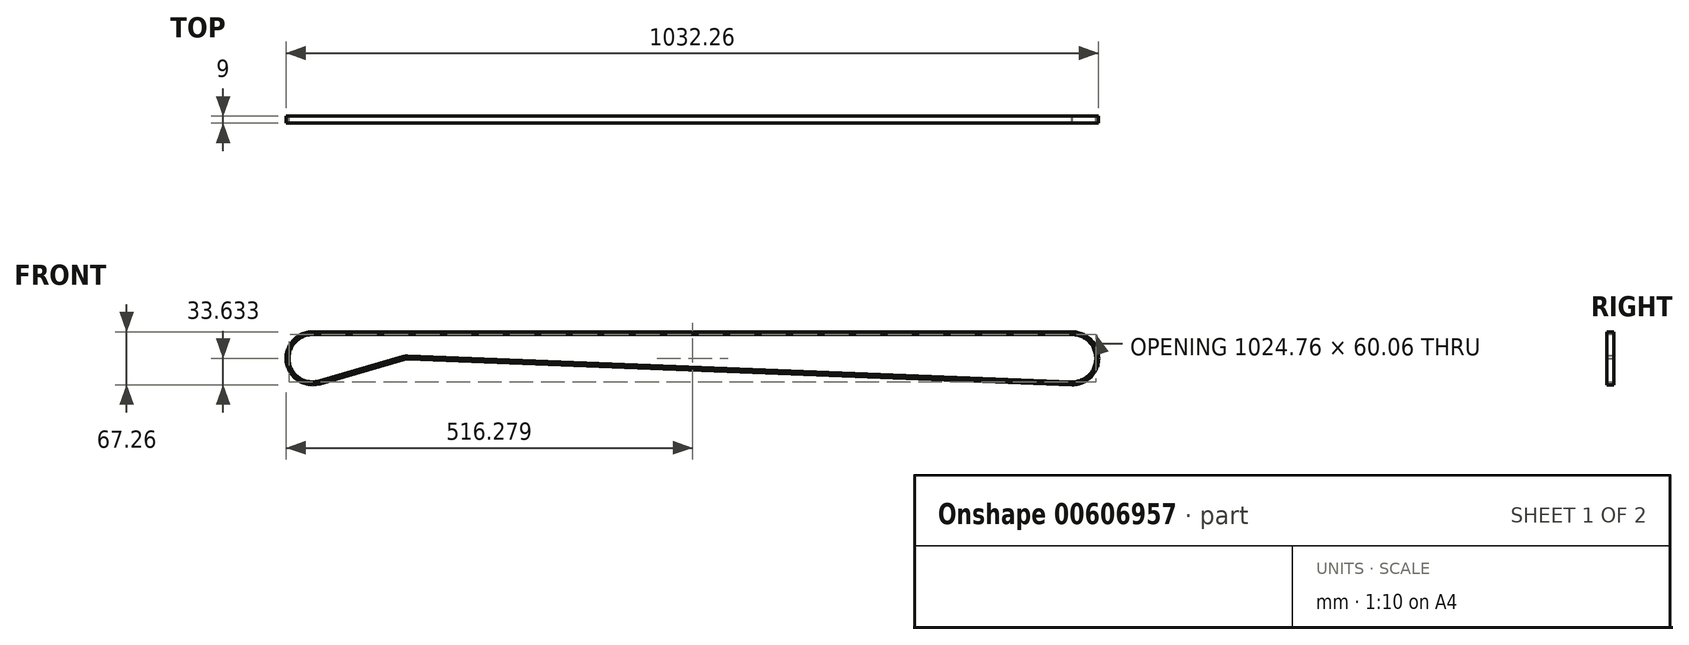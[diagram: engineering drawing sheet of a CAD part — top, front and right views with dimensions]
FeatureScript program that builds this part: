
annotation { "Feature Type Name" : "Feature", "Feature Type Description" : "" }
export const myFeature = defineFeature(function(context is Context, id is Id, definition is map)
    precondition{}
    {
        {
            var Q0;
            Q0=qCreatedBy(makeId("Front.planeOp"),FACE);
            var sketch = newSketch(context, id + "F0", { "sketchPlane" : qUnion([Q0]) });
            skLineSegment(sketch, "E0", {"start": v(118.14, 517.45) * mm, "end": v(118.14, 517.45) * mm});
            skLineSegment(sketch, "E1", {"start": v(-450.16, 1.1) * mm, "end": v(514.84, 1.1) * mm, "construction": true});
            skPoint(sketch, "E2.centerSnap0", {"position": v(32.34, 1.1) * mm});
            skLineSegment(sketch, "E3", {"start": v(-450.16, 32.93) * mm, "end": v(514.84, 32.93) * mm});
            skCircle(sketch, "E4", {"center": v(727.84, 1.1) * mm, "radius": 31.83 * mm});
            skLineSegment(sketch, "E5", {"start": v(514.44, -30.73) * mm, "end": v(-329.54, 2.09) * mm});
            skLineSegment(sketch, "E6", {"start": v(-441.3, -29.47) * mm, "end": v(-334.62, 1.47) * mm});
            skArc(sketch, "E7", {"start": v(-334.62, 1.47) * mm, "mid": v(-328.22, -29.78) * mm, "end": v(-329.54, 2.09) * mm});
            skArc(sketch, "E8", {"start": v(-329.54, 2.09) * mm, "mid": v(-332.1, 1.98) * mm, "end": v(-334.62, 1.47) * mm});
            skLineSegment(sketch, "E9", {"start": v(-450.16, 32.93) * mm, "end": v(-450.16, 32.93) * mm});
            skLineSegment(sketch, "E10", {"start": v(-441.3, -29.47) * mm, "end": v(-441.3, -29.47) * mm});
            skArc(sketch, "E11", {"start": v(-450.16, 32.93) * mm, "mid": v(-481.67, -3.38) * mm, "end": v(-441.3, -29.47) * mm});
            skArc(sketch, "E12", {"start": v(-441.3, -29.47) * mm, "mid": v(-418.65, 5.58) * mm, "end": v(-450.16, 32.93) * mm});
            skArc(sketch, "E13", {"start": v(514.84, 32.93) * mm, "mid": v(483.01, 1.3) * mm, "end": v(514.44, -30.73) * mm});
            skArc(sketch, "E14", {"start": v(514.44, -30.73) * mm, "mid": v(546.67, 0.9) * mm, "end": v(514.84, 32.93) * mm});
            skSolve(sketch);
        }
        {
            var Q0;
            Q0=qCreatedBy(makeId("Right.planeOp"),FACE);
            var sketch = newSketch(context, id + "F1", { "sketchPlane" : qUnion([Q0]) });
            skPoint(sketch, "E15.0", {"position": v(0, 32.93) * mm});
            skLineSegment(sketch, "E16.bottom", {"start": v(4.5, 34.73) * mm, "end": v(-4.5, 34.73) * mm});
            skLineSegment(sketch, "E16.top", {"start": v(4.5, 31.13) * mm, "end": v(-4.5, 31.13) * mm});
            skLineSegment(sketch, "E16.left", {"start": v(4.5, 34.73) * mm, "end": v(4.5, 31.13) * mm});
            skLineSegment(sketch, "E16.right", {"start": v(-4.5, 34.73) * mm, "end": v(-4.5, 31.13) * mm});
            skSolve(sketch);
        }
        {
            var Q0;
            Q0=makeQuery(id+"F1.imprint","IMPRINT",FACE,{"disambiguationData":[TD([[makeQuery(id+"F1.imprint","IMPRINT",EDGE,{"derivedFrom":sQuery(id+"F1.wireOp",EDGE,"E16.bottom")}),1.0]])]});
            var Q1;
            Q1=sQuery(id+"F0.wireOp",EDGE,"E3");
            var Q2;
            Q2=sQuery(id+"F0.wireOp",EDGE,"E11");
            var Q3;
            Q3=sQuery(id+"F0.wireOp",EDGE,"E6");
            var Q4;
            Q4=sQuery(id+"F0.wireOp",EDGE,"E8");
            var Q5;
            Q5=sQuery(id+"F0.wireOp",EDGE,"E5");
            var Q6;
            Q6=sQuery(id+"F0.wireOp",EDGE,"E14");
            sweep(context, id + "F2", {"profiles" : qUnion([Q0]), "path" : qUnion([Q1, Q2, Q3, Q4, Q5, Q6])});
        }
    });
